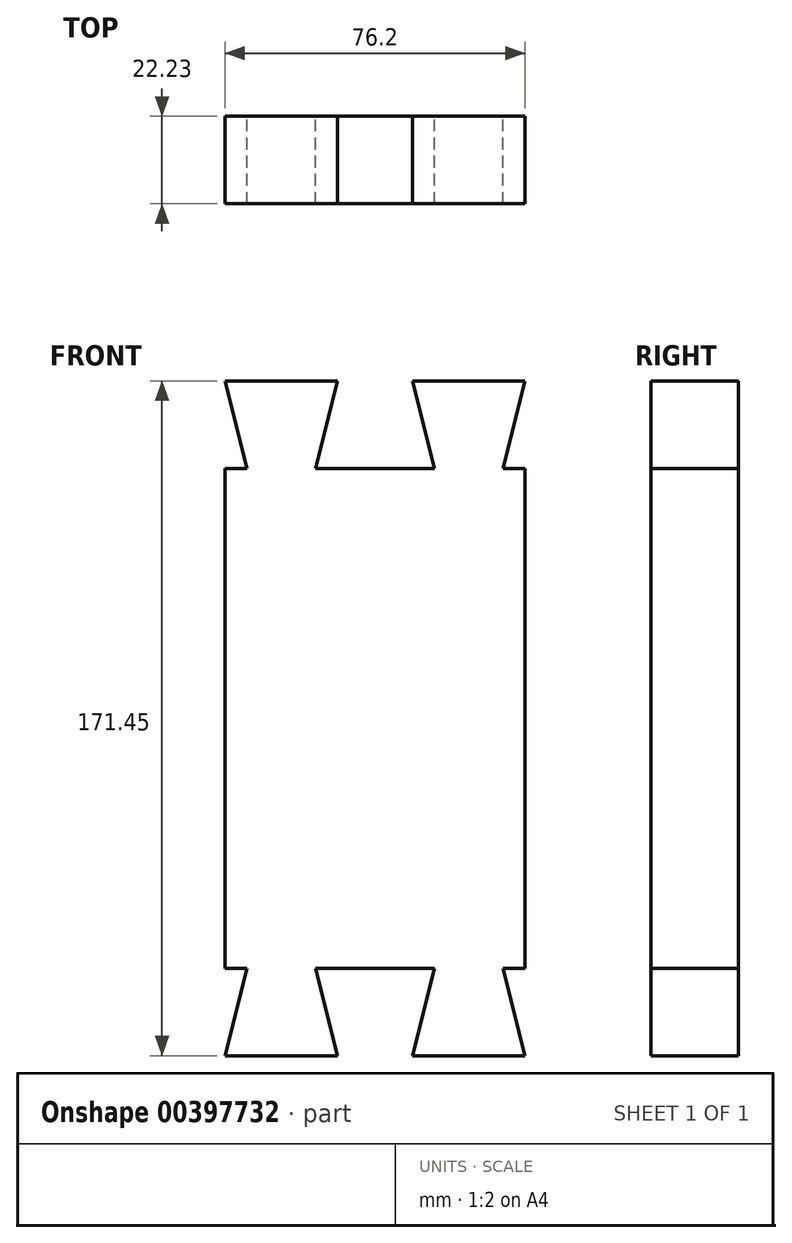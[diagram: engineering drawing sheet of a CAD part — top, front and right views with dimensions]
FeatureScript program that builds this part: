
annotation { "Feature Type Name" : "Feature", "Feature Type Description" : "" }
export const myFeature = defineFeature(function(context is Context, id is Id, definition is map)
    precondition{}
    {
        {
            var Q0;
            Q0=qCreatedBy(makeId("Front.planeOp"),FACE);
            var sketch = newSketch(context, id + "F0", { "sketchPlane" : qUnion([Q0])});
            skLineSegment(sketch, "E0.bottom", {"start": v(0, 0) * mm, "end": v(76.2, 0) * mm});
            skLineSegment(sketch, "E0.top", {"start": v(0, 171.45) * mm, "end": v(76.2, 171.45) * mm});
            skLineSegment(sketch, "E0.left", {"start": v(0, 0) * mm, "end": v(0, 171.45) * mm});
            skLineSegment(sketch, "E0.right", {"start": v(76.2, 0) * mm, "end": v(76.2, 171.45) * mm});
            skSolve(sketch);
        }
        {
            var Q0;
            Q0=makeQuery(id+"F0.imprint","IMPRINT",FACE,{"disambiguationData":[TD([[makeQuery(id+"F0.imprint","IMPRINT",EDGE,{"derivedFrom":sQuery(id+"F0.wireOp",EDGE,"E0.bottom")}),1.0]])]});
            extrude(context, id + "F1", {"entities" : qUnion([Q0]), "depth" : 22.22 * mm});
        }
        {
            var Q0;
            Q0=qCreatedBy(makeId("Front.planeOp"),FACE);
            var sketch = newSketch(context, id + "F2", { "sketchPlane" : qUnion([Q0])});
            skLineSegment(sketch, "E1", {"start": v(0, 171.45) * mm, "end": v(5.54, 149.23) * mm});
            skLineSegment(sketch, "E2", {"start": v(5.54, 149.23) * mm, "end": v(0, 149.23) * mm});
            skLineSegment(sketch, "E3", {"start": v(0, 149.23) * mm, "end": v(0, 171.45) * mm});
            skLineSegment(sketch, "E4", {"start": v(5.54, 149.23) * mm, "end": v(23.03, 149.23) * mm, "construction": true});
            skLineSegment(sketch, "E5", {"start": v(23.03, 149.23) * mm, "end": v(28.58, 171.45) * mm});
            skLineSegment(sketch, "E6", {"start": v(76.2, 171.45) * mm, "end": v(70.66, 149.23) * mm});
            skLineSegment(sketch, "E7", {"start": v(70.66, 149.22) * mm, "end": v(76.2, 149.22) * mm});
            skLineSegment(sketch, "E8", {"start": v(76.2, 149.23) * mm, "end": v(76.2, 171.45) * mm});
            skLineSegment(sketch, "E9", {"start": v(70.66, 149.23) * mm, "end": v(53.17, 149.23) * mm, "construction": true});
            skLineSegment(sketch, "E10", {"start": v(53.17, 149.23) * mm, "end": v(47.62, 171.45) * mm});
            skLineSegment(sketch, "E11", {"start": v(47.62, 171.45) * mm, "end": v(28.57, 171.45) * mm});
            skLineSegment(sketch, "E12", {"start": v(47.62, 171.45) * mm, "end": v(76.2, 171.45) * mm});
            skLineSegment(sketch, "E13", {"start": v(28.57, 171.45) * mm, "end": v(47.62, 171.45) * mm});
            skLineSegment(sketch, "E14", {"start": v(23.03, 149.23) * mm, "end": v(53.17, 149.23) * mm});
            skLineSegment(sketch, "E15", {"start": v(0, 0) * mm, "end": v(5.54, 22.23) * mm});
            skLineSegment(sketch, "E16", {"start": v(5.54, 22.23) * mm, "end": v(0, 22.23) * mm});
            skLineSegment(sketch, "E17", {"start": v(0, 22.23) * mm, "end": v(0, 0) * mm});
            skLineSegment(sketch, "E18", {"start": v(23.03, 22.23) * mm, "end": v(28.58, 0) * mm});
            skLineSegment(sketch, "E19", {"start": v(28.58, 0) * mm, "end": v(47.63, 0) * mm});
            skLineSegment(sketch, "E20", {"start": v(47.63, 0) * mm, "end": v(53.17, 22.23) * mm});
            skLineSegment(sketch, "E21", {"start": v(53.17, 22.23) * mm, "end": v(23.03, 22.23) * mm});
            skLineSegment(sketch, "E22", {"start": v(76.2, 0) * mm, "end": v(70.66, 22.23) * mm});
            skLineSegment(sketch, "E23", {"start": v(70.66, 22.23) * mm, "end": v(76.2, 22.23) * mm});
            skLineSegment(sketch, "E24", {"start": v(76.2, 22.23) * mm, "end": v(76.2, 0) * mm});
            skLineSegment(sketch, "E25", {"start": v(5.54, 22.23) * mm, "end": v(23.03, 22.23) * mm, "construction": true});
            skLineSegment(sketch, "E26", {"start": v(53.17, 22.23) * mm, "end": v(70.66, 22.23) * mm, "construction": true});
            skSolve(sketch);
        }
        {
            var Q0;
            Q0=makeQuery(id+"F2.imprint","IMPRINT",FACE,{"disambiguationData":[TD([[makeQuery(id+"F2.imprint","IMPRINT",EDGE,{"derivedFrom":sQuery(id+"F2.wireOp",EDGE,"E5")}),-1.0]])]});
            var Q1;
            Q1=makeQuery(id+"F2.imprint","IMPRINT",FACE,{"disambiguationData":[TD([[makeQuery(id+"F2.imprint","IMPRINT",EDGE,{"derivedFrom":sQuery(id+"F2.wireOp",EDGE,"E6")}),1.0]])]});
            var Q2;
            Q2=makeQuery(id+"F2.imprint","IMPRINT",FACE,{"disambiguationData":[TD([[makeQuery(id+"F2.imprint","IMPRINT",EDGE,{"derivedFrom":sQuery(id+"F2.wireOp",EDGE,"E1")}),-1.0]])]});
            var Q3;
            Q3=makeQuery(id+"F2.imprint","IMPRINT",FACE,{"disambiguationData":[TD([[makeQuery(id+"F2.imprint","IMPRINT",EDGE,{"derivedFrom":sQuery(id+"F2.wireOp",EDGE,"E22")}),-1.0]])]});
            var Q4;
            Q4=makeQuery(id+"F2.imprint","IMPRINT",FACE,{"disambiguationData":[TD([[makeQuery(id+"F2.imprint","IMPRINT",EDGE,{"derivedFrom":sQuery(id+"F2.wireOp",EDGE,"E18")}),1.0]])]});
            var Q5;
            Q5=makeQuery(id+"F2.imprint","IMPRINT",FACE,{"disambiguationData":[TD([[makeQuery(id+"F2.imprint","IMPRINT",EDGE,{"derivedFrom":sQuery(id+"F2.wireOp",EDGE,"E15")}),1.0]])]});
            extrude(context, id + "F3", {"entities" : qUnion([Q0, Q1, Q2, Q3, Q4, Q5]), "operationType" : NewBodyOperationType.REMOVE, "endBound" : BoundingType.THROUGH_ALL, "depth" : 25.4 * mm});
        }
    });
